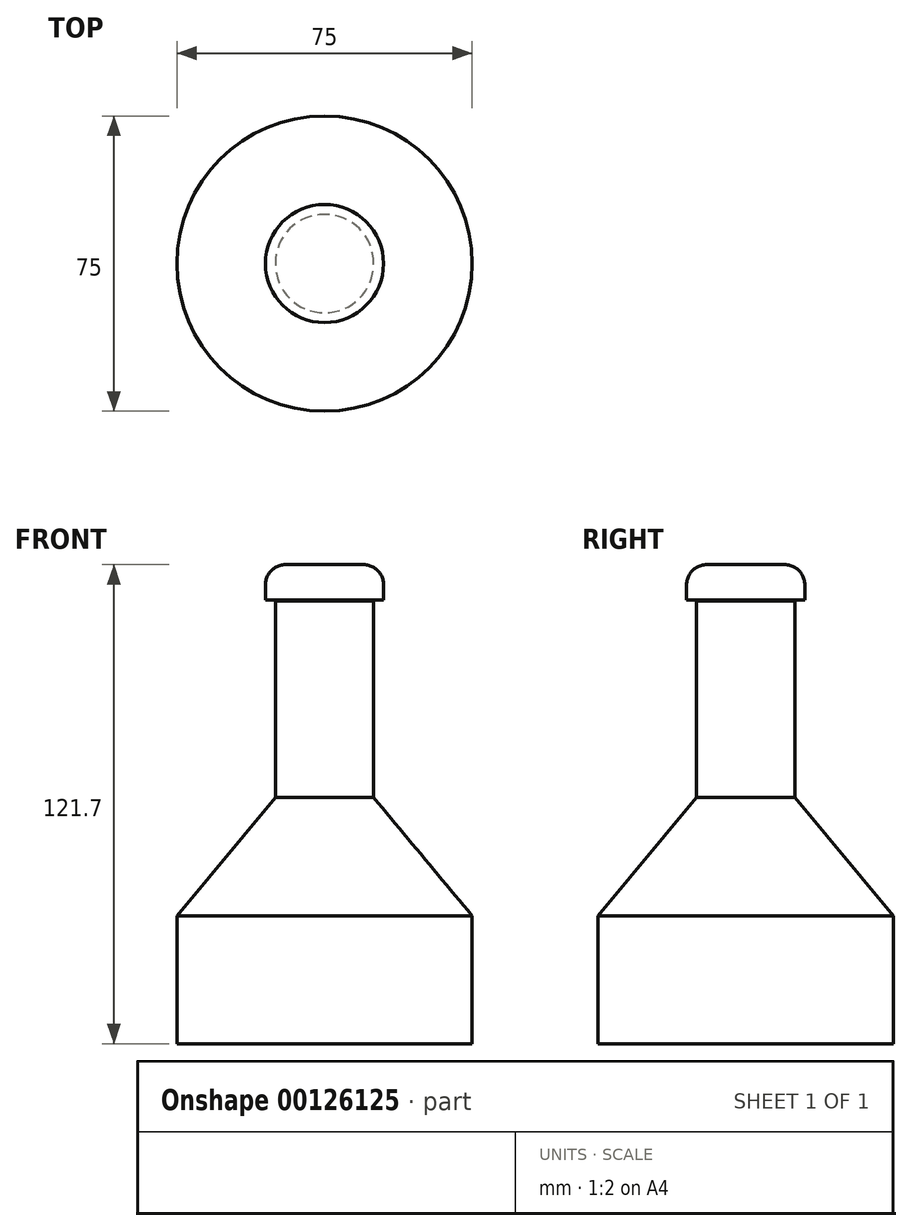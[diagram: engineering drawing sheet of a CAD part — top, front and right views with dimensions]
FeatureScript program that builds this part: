
annotation { "Feature Type Name" : "Feature", "Feature Type Description" : "" }
export const myFeature = defineFeature(function(context is Context, id is Id, definition is map)
    precondition{}
    {
        {
            var Q0;
            Q0=qCreatedBy(makeId("Top.planeOp"),FACE);
            cPlane(context, id + "F0", {"entities" : qUnion([Q0]), "cplaneType" : CPlaneType.OFFSET, "offset" : 50 * mm, "width" : 152.4 * mm, "height" : 152.4 * mm});
        }
        {
            var Q0;
            Q0=qCreatedBy(makeId("Top.planeOp"),FACE);
            cPlane(context, id + "F1", {"entities" : qUnion([Q0]), "cplaneType" : CPlaneType.OFFSET, "offset" : 50 * mm, "oppositeDirection" : true, "width" : 152.4 * mm, "height" : 152.4 * mm});
        }
        {
            var Q0;
            Q0=qCreatedBy(id+"F1.planeOp",FACE);
            var sketch = newSketch(context, id + "F2", { "sketchPlane" : qUnion([Q0])});
            skCircle(sketch, "E0", {"center": v(0, 0) * mm, "radius": 37.5 * mm});
            skSolve(sketch);
        }
        {
            var Q0;
            Q0=qCreatedBy(id+"F1.planeOp",FACE);
            var sketch = newSketch(context, id + "F3", { "sketchPlane" : qUnion([Q0])});
            skSolve(sketch);
        }
        {
            var Q0;
            Q0=qCreatedBy(id+"F0.planeOp",FACE);
            var sketch = newSketch(context, id + "F4", { "sketchPlane" : qUnion([Q0])});
            skCircle(sketch, "E1", {"center": v(0, 0) * mm, "radius": 12.5 * mm});
            skSolve(sketch);
        }
        {
            var Q0;
            Q0=qCreatedBy(id+"F0.planeOp",FACE);
            cPlane(context, id + "F5", {"entities" : qUnion([Q0]), "cplaneType" : CPlaneType.OFFSET, "offset" : 12.7 * mm, "width" : 152.4 * mm, "height" : 152.4 * mm});
        }
        {
            var Q0;
            Q0=qCreatedBy(id+"F5.planeOp",FACE);
            var sketch = newSketch(context, id + "F6", { "sketchPlane" : qUnion([Q0])});
            skCircle(sketch, "E2", {"center": v(0, 0) * mm, "radius": 15 * mm});
            skSolve(sketch);
        }
        {
            var Q0;
            Q0 = qSketchRegion(id + "F6", true);
            extrude(context, id + "F7", {"entities" : qUnion([Q0]), "depth" : 9 * mm});
        }
        {
            var Q0;
            Q0=makeQuery(id+"F7.opExtrude","CAP_EDGE",EDGE,{"disambiguationData":[OSD([sQuery(id+"F6.wireOp",EDGE,"E2")])],"isStart":false});
            fillet(context, id + "F8", {"entities" : qUnion([Q0]), "radius" : 5.08 * mm, "tangentPropagation" : true, "allowEdgeOverflow" : false});
        }
        {
            var Q0;
            Q0=qCreatedBy(makeId("Top.planeOp"),FACE);
            cPlane(context, id + "F9", {"entities" : qUnion([Q0]), "cplaneType" : CPlaneType.OFFSET, "offset" : 17.5 * mm, "oppositeDirection" : true, "width" : 152.4 * mm, "height" : 152.4 * mm});
        }
        {
            var Q0;
            Q0=qCreatedBy(id+"F9.planeOp",FACE);
            var sketch = newSketch(context, id + "F10", { "sketchPlane" : qUnion([Q0])});
            skCircle(sketch, "E3", {"center": v(0, 0) * mm, "radius": 37.5 * mm});
            skSolve(sketch);
        }
        {
            var Q0;
            Q0=qCreatedBy(makeId("Top.planeOp"),FACE);
            cPlane(context, id + "F11", {"entities" : qUnion([Q0]), "cplaneType" : CPlaneType.OFFSET, "offset" : 12.5 * mm, "width" : 152.4 * mm, "height" : 152.4 * mm});
        }
        {
            var Q0;
            Q0=qCreatedBy(id+"F11.planeOp",FACE);
            var sketch = newSketch(context, id + "F12", { "sketchPlane" : qUnion([Q0])});
            skCircle(sketch, "E4", {"center": v(0, 0) * mm, "radius": 12.5 * mm});
            skSolve(sketch);
        }
        {
            var Q0;
            Q0 = qSketchRegion(id + "F3", true);
            var Q1;
            Q1=makeQuery(id+"F2.imprint","IMPRINT",FACE,{"disambiguationData":[TD([[makeQuery(id+"F2.imprint","IMPRINT",EDGE,{"derivedFrom":sQuery(id+"F2.wireOp",EDGE,"E0")}),1.0]])]});
            extrude(context, id + "F13", {"entities" : qUnion([Q0, Q1]), "depth" : 32.5 * mm});
        }
        {
            var Q1;
            Q1=makeQuery(id+"F10.imprint","IMPRINT",FACE,{"disambiguationData":[TD([[makeQuery(id+"F10.imprint","IMPRINT",EDGE,{"derivedFrom":sQuery(id+"F10.wireOp",EDGE,"E3")}),1.0]])]});
            var Q2;
            Q2=makeQuery(id+"F12.imprint","IMPRINT",FACE,{"disambiguationData":[TD([[makeQuery(id+"F12.imprint","IMPRINT",EDGE,{"derivedFrom":sQuery(id+"F12.wireOp",EDGE,"E4")}),1.0]])]});
            loft(context, id + "F14", {"operationType" : NewBodyOperationType.ADD, "sheetProfilesArray" : [{ "sheetProfileEntities" : qUnion([Q1]) }, { "sheetProfileEntities" : qUnion([Q2]) }]});
        }
        {
            var Q0;
            Q0 = qSketchRegion(id + "F12", true);
            extrude(context, id + "F15", {"entities" : qUnion([Q0]), "operationType" : NewBodyOperationType.ADD, "depth" : 37.5 * mm});
        }
        {
            var Q0;
            Q0=makeQuery(id+"F4.imprint","IMPRINT",FACE,{"disambiguationData":[TD([[makeQuery(id+"F4.imprint","IMPRINT",EDGE,{"derivedFrom":sQuery(id+"F4.wireOp",EDGE,"E1")}),1.0]])]});
            extrude(context, id + "F16", {"entities" : qUnion([Q0]), "operationType" : NewBodyOperationType.ADD, "depth" : 12.5 * mm});
        }
    });
